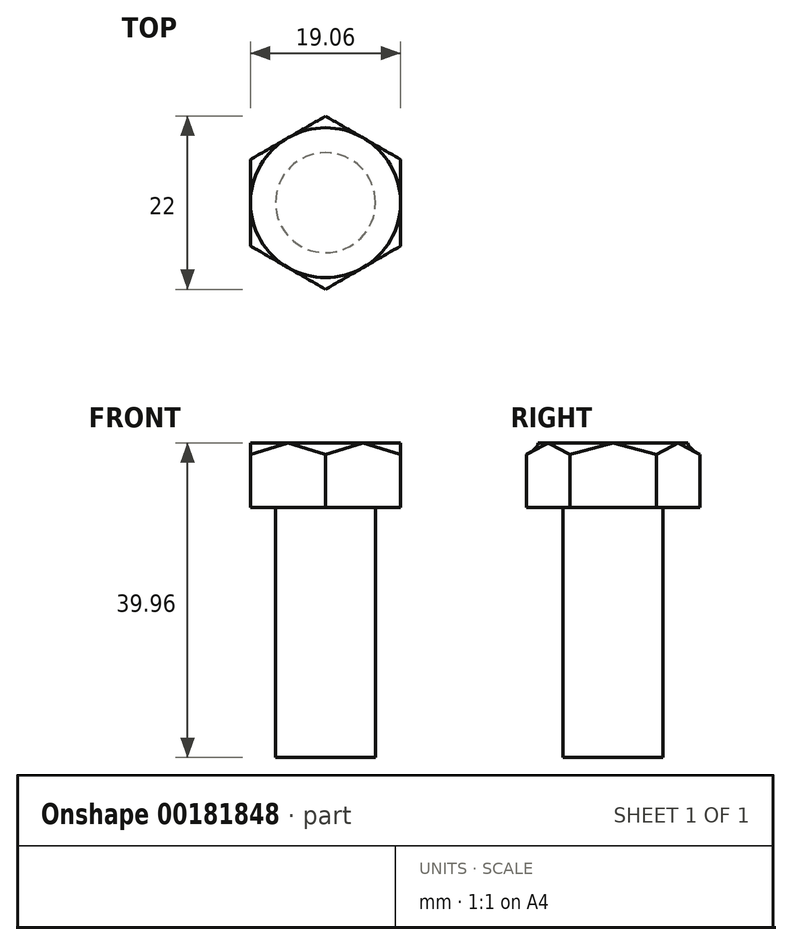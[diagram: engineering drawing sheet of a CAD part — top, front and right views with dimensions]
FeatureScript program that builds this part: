
annotation { "Feature Type Name" : "Feature", "Feature Type Description" : "" }
export const myFeature = defineFeature(function(context is Context, id is Id, definition is map)
    precondition{}
    {
        {
            var Q0;
            Q0=qCreatedBy(makeId("Top.planeOp"),FACE);
            var sketch = newSketch(context, id + "F0", { "sketchPlane" : qUnion([Q0])});
            skCircle(sketch, "E0", {"center": v(0, 0) * mm, "radius": 6.35 * mm});
            skSolve(sketch);
        }
        {
            var Q0;
            Q0 = qSketchRegion(id + "F0", true);
            extrude(context, id + "F1", {"entities" : qUnion([Q0]), "endBound" : BoundingType.SYMMETRIC, "depth" : 31.75 * mm});
        }
        {
            var Q0;
            Q0=makeQuery(id+"F1.opExtrude","CAP_FACE",FACE,{"disambiguationData":[OSD([sQuery(id+"F0.wireOp",EDGE,"E0")])],"isStart":false});
            var sketch = newSketch(context, id + "F2", { "sketchPlane" : qUnion([Q0])});
            skCircle(sketch, "E1.cCircle", {"center": v(0, 0) * mm, "radius": 9.53 * mm, "construction": true});
            skLineSegment(sketch, "E1.0", {"start": v(9.53, 5.5) * mm, "end": v(9.53, -5.5) * mm});
            skLineSegment(sketch, "E1.1", {"start": v(9.53, -5.5) * mm, "end": v(0, -11) * mm});
            skLineSegment(sketch, "E1.2", {"start": v(0, -11) * mm, "end": v(-9.52, -5.5) * mm});
            skLineSegment(sketch, "E1.3", {"start": v(-9.52, -5.5) * mm, "end": v(-9.53, 5.5) * mm});
            skLineSegment(sketch, "E1.4", {"start": v(-9.53, 5.5) * mm, "end": v(0, 11) * mm});
            skLineSegment(sketch, "E1.5", {"start": v(0, 11) * mm, "end": v(9.52, 5.5) * mm});
            skPoint(sketch, "E1.0.midPoint", {"position": v(9.53, 0) * mm});
            skSolve(sketch);
        }
        {
            var Q0;
            Q0 = qSketchRegion(id + "F2", true);
            extrude(context, id + "F3", {"entities" : qUnion([Q0]), "operationType" : NewBodyOperationType.ADD, "depth" : 8.2 * mm});
        }
        {
            var Q0;
            Q0=qCreatedBy(makeId("Right.planeOp"),FACE);
            var sketch = newSketch(context, id + "F4", { "sketchPlane" : qUnion([Q0])});
            skLineSegment(sketch, "E2", {"start": v(0, -40.35) * mm, "end": v(0, 43.33) * mm, "construction": true});
            skSolve(sketch);
        }
        {
            var Q0;
            Q0=makeQuery(id+"F3.opExtrude","SWEPT_FACE",FACE,{"disambiguationData":[OSD([sQuery(id+"F2.wireOp",EDGE,"E1.0")])]});
            var sketch = newSketch(context, id + "F5", { "sketchPlane" : qUnion([Q0])});
            skLineSegment(sketch, "E3", {"start": v(0, 24.08) * mm, "end": v(5.5, 22.6) * mm});
            skLineSegment(sketch, "E4", {"start": v(5.5, 22.6) * mm, "end": v(5.5, 24.08) * mm});
            skLineSegment(sketch, "E5", {"start": v(5.5, 24.08) * mm, "end": v(0, 24.08) * mm});
            skSolve(sketch);
        }
        {
            var Q0;
            Q0=makeQuery(id+"F5.imprint","IMPRINT",FACE,{"disambiguationData":[TD([[makeQuery(id+"F5.imprint","IMPRINT",EDGE,{"derivedFrom":sQuery(id+"F5.wireOp",EDGE,"E3")}),1.0]])]});
            var Q1;
            Q1=sQuery(id+"F4.wireOp",EDGE,"E2");
            revolve(context, id + "F6", {"operationType" : NewBodyOperationType.REMOVE, "entities" : qUnion([Q0]), "axis" : qUnion([Q1]), "revolveType" : RevolveType.FULL});
        }
    });
